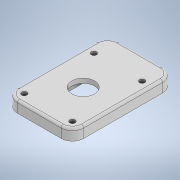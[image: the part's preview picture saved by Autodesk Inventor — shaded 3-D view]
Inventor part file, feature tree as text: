
AUTODESK INVENTOR PART (.ipt)
format: ipt  version: 2022 (Build 260153000, 153)  size: 182,272 bytes
history: native  units: in
note: dims shown in document units (in); Inventor stores cm internally (conversion verified against a paired STEP export)
features: extrude x2, fillet x2, sketch x2, projected_geometry x1
ambient origin geometry x8: Origin, YZ Plane, XZ Plane, XY Plane, X Axis, Y Axis, Z Axis, Center Point
bodies: Solid1 (feature_tree)
feature tree (7):
  extrude  "Extrusion1"  Depth=0.33in
  extrude  "Extrusion2"  Depth=0.66in
  fillet  "Fillet1"  Radius=1.133in
  fillet  "Fillet2"  Radius=0.2in
  sketch  "Sketch1"  dims[d0=0.45in d1=0.33in]
  sketch  "Sketch2"  dims[d2=0.5665in d3=0.66in d4=1.133in d5=0.2in d6=0.2in d7=0.2in d8=0.2in d9=0.1181in d10=0.1181in d11=0.1181in d12=0.1181in d13=0.2in d14=0.2in d15=0.15in d16=0.0in d17=0.5in d18=0.1in d19=0.0in d20=0.25in d21=0.05in d22=0.3in]
  projected_geometry  "Projected Loop1"
